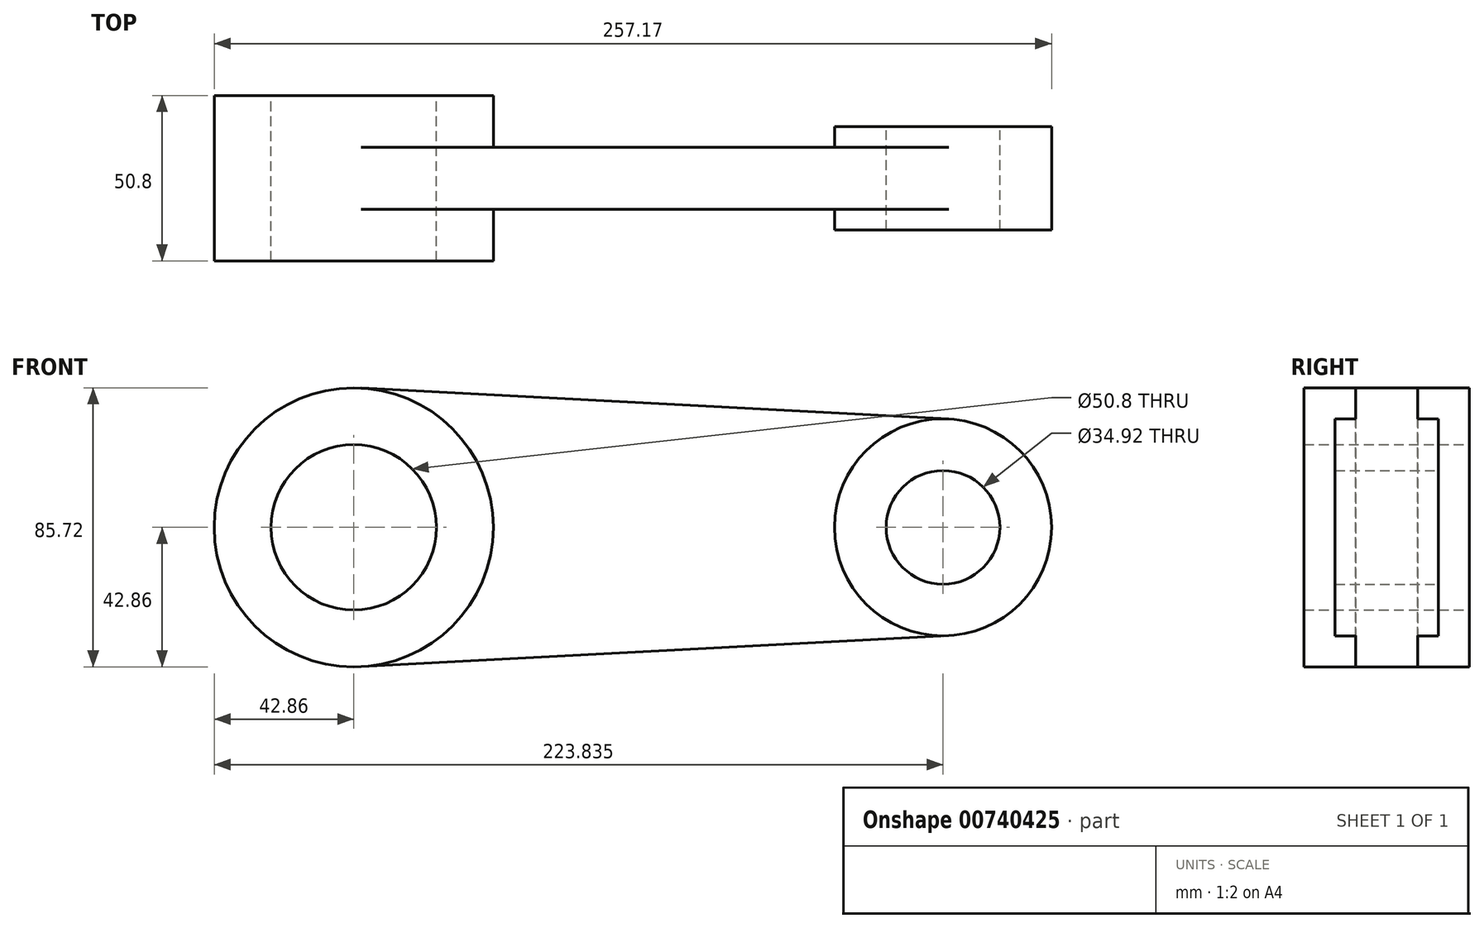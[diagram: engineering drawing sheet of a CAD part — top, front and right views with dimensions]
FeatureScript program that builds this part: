
annotation { "Feature Type Name" : "Feature", "Feature Type Description" : "" }
export const myFeature = defineFeature(function(context is Context, id is Id, definition is map)
    precondition{}
    {
        {
            var Q0;
            Q0=qCreatedBy(makeId("Front.planeOp"),FACE);
            var sketch = newSketch(context, id + "F0", { "sketchPlane" : qUnion([Q0])});
            skCircle(sketch, "E0", {"center": v(0, 0) * mm, "radius": 25.4 * mm});
            skCircle(sketch, "E1", {"center": v(0, 0) * mm, "radius": 42.86 * mm});
            skCircle(sketch, "E2", {"center": v(180.98, 0) * mm, "radius": 17.46 * mm});
            skCircle(sketch, "E3", {"center": v(180.98, 0) * mm, "radius": 33.34 * mm});
            skLineSegment(sketch, "E4", {"start": v(2.26, -42.8) * mm, "end": v(182.73, -33.3) * mm});
            skLineSegment(sketch, "E5", {"start": v(2.26, 42.8) * mm, "end": v(182.73, 33.3) * mm});
            skSolve(sketch);
        }
        {
            var Q0;
            Q0=makeQuery(id+"F0.imprint","IMPRINT",FACE,{"disambiguationData":[TD([[makeQuery(id+"F0.imprint","IMPRINT",EDGE,{"derivedFrom":sQuery(id+"F0.wireOp",EDGE,"E0")}),-1.0]])]});
            extrude(context, id + "F1", {"entities" : qUnion([Q0]), "endBound" : BoundingType.SYMMETRIC, "depth" : 50.8 * mm});
        }
        {
            var Q0;
            {var subQ0=sQuery(id+"F0.wireOp",EDGE,"eR6GLvmT-agu1-3Djh-gmzt-1HRNs2KsTib9");var subQ1=sQuery(id+"F0.wireOp",EDGE,"E1");var subQ2=makeQuery(id+"F0.imprint","INTERSECT",VERTEX,{"disambiguationData":[OD(1.0)],"derivedFrom":[subQ1,subQ0]});Q0=makeQuery(id+"F0.imprint","IMPRINT",FACE,{"disambiguationData":[TD([[makeQuery(id+"F0.imprint","IMPRINT",EDGE,{"disambiguationData":[TD([[subQ2,1.0]])],"derivedFrom":subQ1}),-1.0]])]});}
            extrude(context, id + "F2", {"entities" : qUnion([Q0]), "operationType" : NewBodyOperationType.ADD, "endBound" : BoundingType.SYMMETRIC, "depth" : 19.05 * mm});
        }
        {
            var Q0;
            Q0=makeQuery(id+"F0.imprint","IMPRINT",FACE,{"disambiguationData":[TD([[makeQuery(id+"F0.imprint","IMPRINT",EDGE,{"derivedFrom":sQuery(id+"F0.wireOp",EDGE,"E2")}),-1.0]])]});
            extrude(context, id + "F3", {"entities" : qUnion([Q0]), "operationType" : NewBodyOperationType.ADD, "endBound" : BoundingType.SYMMETRIC, "depth" : 31.75 * mm});
        }
    });
